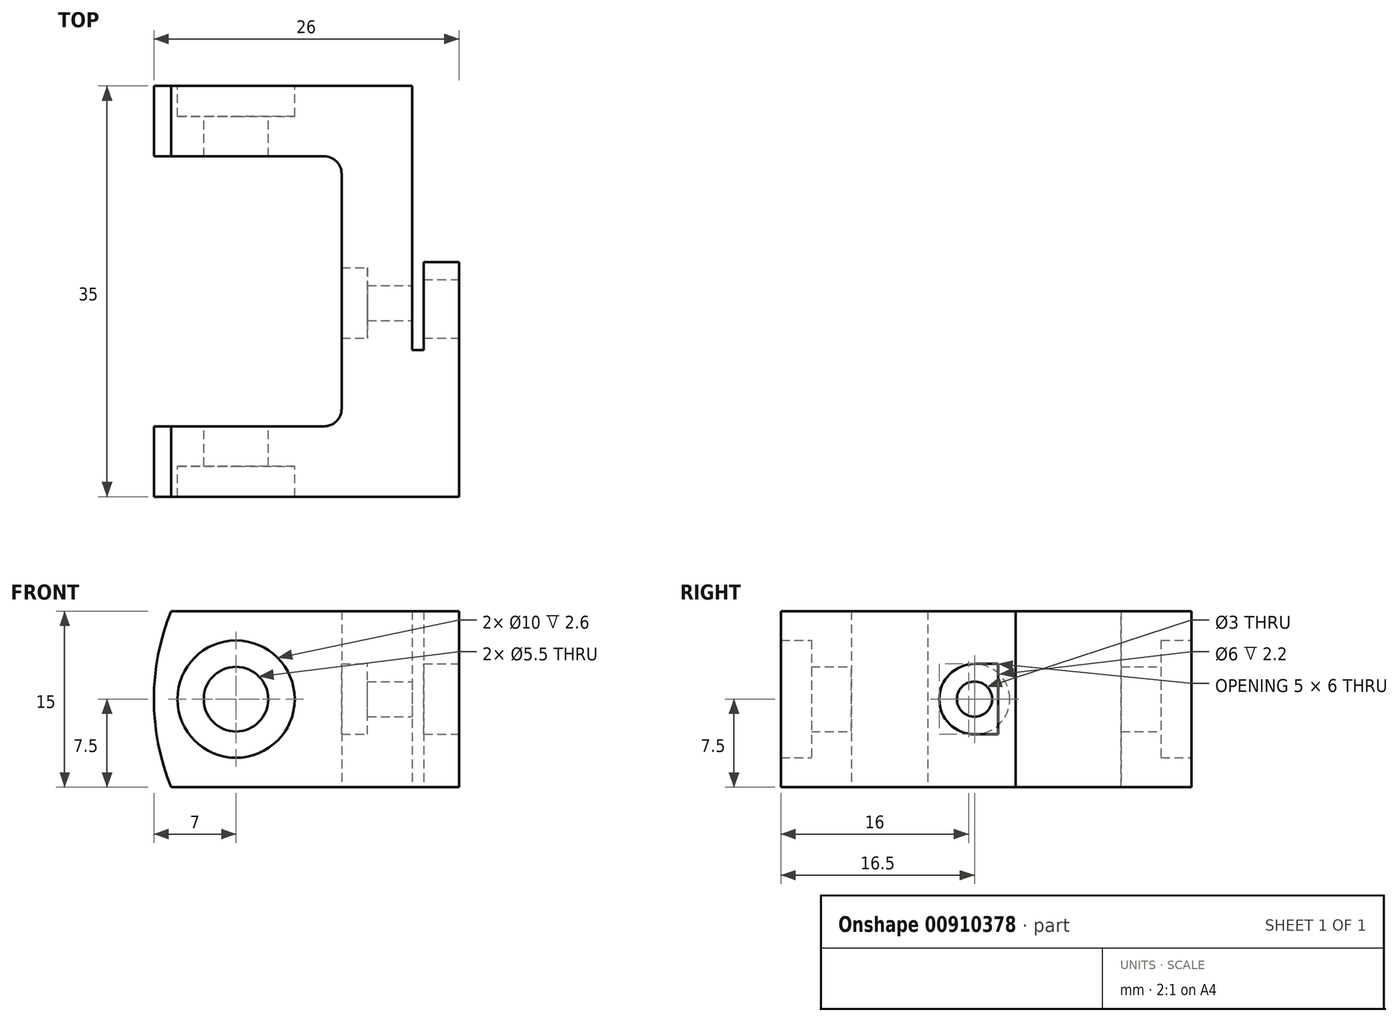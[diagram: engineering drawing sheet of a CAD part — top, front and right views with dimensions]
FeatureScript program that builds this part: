
annotation { "Feature Type Name" : "Feature", "Feature Type Description" : "" }
export const myFeature = defineFeature(function(context is Context, id is Id, definition is map)
    precondition{}
    {
        {
            var Q0;
            Q0=qCreatedBy(makeId("Top.planeOp"),FACE);
            var sketch = newSketch(context, id + "F0", { "sketchPlane" : qUnion([Q0])});
            skLineSegment(sketch, "E0", {"start": v(-16, 12.5) * mm, "end": v(-1.5, 12.5) * mm});
            skLineSegment(sketch, "E1", {"start": v(0, 11) * mm, "end": v(0, -9) * mm});
            skLineSegment(sketch, "E2", {"start": v(-1.5, -10.5) * mm, "end": v(-16, -10.5) * mm});
            skLineSegment(sketch, "E3", {"start": v(-16, -10.5) * mm, "end": v(-16, -16.5) * mm});
            skLineSegment(sketch, "E4", {"start": v(-16, -16.5) * mm, "end": v(10, -16.5) * mm});
            skLineSegment(sketch, "E5", {"start": v(10, -16.5) * mm, "end": v(10, 3.5) * mm});
            skLineSegment(sketch, "E6", {"start": v(10, 3.5) * mm, "end": v(7, 3.5) * mm});
            skLineSegment(sketch, "E7", {"start": v(7, 3.5) * mm, "end": v(7, -4) * mm});
            skLineSegment(sketch, "E8", {"start": v(7, -4) * mm, "end": v(6, -4) * mm});
            skLineSegment(sketch, "E9", {"start": v(6, -4) * mm, "end": v(6, 18.5) * mm});
            skLineSegment(sketch, "E10", {"start": v(6, 18.5) * mm, "end": v(-16, 18.5) * mm});
            skLineSegment(sketch, "E11", {"start": v(-16, 18.5) * mm, "end": v(-16, 12.5) * mm});
            skPoint(sketch, "E12.visualSharp", {"position": v(0, 12.5) * mm});
            skArc(sketch, "E12.filletArc", {"start": v(0, 11) * mm, "mid": v(-0.44, 12.06) * mm, "end": v(-1.5, 12.5) * mm});
            skPoint(sketch, "E13.visualSharp", {"position": v(0, -10.5) * mm});
            skArc(sketch, "E13.filletArc", {"start": v(-1.5, -10.5) * mm, "mid": v(-0.44, -10.06) * mm, "end": v(0, -9) * mm});
            skSolve(sketch);
        }
        {
            var Q0;
            Q0 = qSketchRegion(id + "F0", true);
            extrude(context, id + "F1", {"entities" : qUnion([Q0]), "depth" : 15 * mm, "offsetDistance" : 25.4 * mm, "symmetric" : true});
        }
        {
            var Q0;
            Q0=makeQuery(id+"F1.opExtrude","SWEPT_FACE",FACE,{"disambiguationData":[OSD([sQuery(id+"F0.wireOp",EDGE,"E1")])]});
            var sketch = newSketch(context, id + "F2", { "sketchPlane" : qUnion([Q0])});
            skPoint(sketch, "E14", {"position": v(0, 0) * mm});
            skSolve(sketch);
        }
        {
            var Q0;
            Q0=sQuery(id+"F2.wireOp",VERTEX,"E14");
            var Q1;
            Q1=makeQuery(id+"F1.opExtrude","SWEPT_BODY",BODY,{"disambiguationData":[OSD([sQuery(id+"F0.wireOp",EDGE,"E0"),sQuery(id+"F0.wireOp",EDGE,"E1"),sQuery(id+"F0.wireOp",EDGE,"E2"),sQuery(id+"F0.wireOp",EDGE,"E3"),sQuery(id+"F0.wireOp",EDGE,"E4"),sQuery(id+"F0.wireOp",EDGE,"E5"),sQuery(id+"F0.wireOp",EDGE,"E6"),sQuery(id+"F0.wireOp",EDGE,"E7"),sQuery(id+"F0.wireOp",EDGE,"E8"),sQuery(id+"F0.wireOp",EDGE,"E9"),sQuery(id+"F0.wireOp",EDGE,"E10"),sQuery(id+"F0.wireOp",EDGE,"E11"),sQuery(id+"F0.wireOp",EDGE,"E12.filletArc"),sQuery(id+"F0.wireOp",EDGE,"E13.filletArc")])]});
            hole(context, id + "F3", {"style" : HoleStyle.C_BORE, "endStyle" : HoleEndStyle.THROUGH, "holeDiameter" : 3 * mm, "cBoreDiameter" : 6 * mm, "cBoreDepth" : 2.2 * mm, "majorDiameter" : 6.35 * mm, "isTappedThrough" : true, "tappedDepth" : 12.7 * mm, "tapClearance" : 3, "locations" : qUnion([Q0]), "scope" : qUnion([Q1])});
        }
        {
            var Q0;
            Q0=makeQuery(id+"F1.opExtrude","SWEPT_FACE",FACE,{"disambiguationData":[OSD([sQuery(id+"F0.wireOp",EDGE,"E5")])]});
            var sketch = newSketch(context, id + "F4", { "sketchPlane" : qUnion([Q0])});
            skArc(sketch, "E15", {"start": v(0, 3) * mm, "mid": v(-3, 0) * mm, "end": v(0, -3) * mm});
            skLineSegment(sketch, "E16", {"start": v(0, 3) * mm, "end": v(2, 3) * mm});
            skLineSegment(sketch, "E17", {"start": v(2, 3) * mm, "end": v(2, -3) * mm});
            skLineSegment(sketch, "E18", {"start": v(2, -3) * mm, "end": v(0, -3) * mm});
            skSolve(sketch);
        }
        {
            var Q0;
            Q0 = qSketchRegion(id + "F4", true);
            var Q1;
            Q1=makeQuery(id+"F1.opExtrude","SWEPT_FACE",FACE,{"disambiguationData":[OSD([sQuery(id+"F0.wireOp",EDGE,"E7")])]});
            extrude(context, id + "F5", {"entities" : qUnion([Q0]), "operationType" : NewBodyOperationType.REMOVE, "endBound" : BoundingType.UP_TO_SURFACE, "oppositeDirection" : true, "depth" : 25.4 * mm, "endBoundEntityFace" : qUnion([Q1]), "offsetDistance" : 25.4 * mm});
        }
        {
            var Q0;
            Q0=qCreatedBy(makeId("Top.planeOp"),FACE);
            var sketch = newSketch(context, id + "F6", { "sketchPlane" : qUnion([Q0])});
            skLineSegment(sketch, "E19", {"start": v(-4, -16.5) * mm, "end": v(-4, -13.9) * mm});
            skLineSegment(sketch, "E20", {"start": v(-4, -13.9) * mm, "end": v(-6.25, -13.9) * mm});
            skLineSegment(sketch, "E21", {"start": v(-6.25, -13.9) * mm, "end": v(-6.25, 15.9) * mm});
            skLineSegment(sketch, "E22", {"start": v(-6.25, 15.9) * mm, "end": v(-4, 15.9) * mm});
            skLineSegment(sketch, "E23", {"start": v(-4, 15.9) * mm, "end": v(-4, 18.5) * mm});
            skLineSegment(sketch, "E24", {"start": v(-4, 18.5) * mm, "end": v(-9, 18.5) * mm});
            skLineSegment(sketch, "E25", {"start": v(-9, 18.5) * mm, "end": v(-9, -16.5) * mm});
            skLineSegment(sketch, "E26", {"start": v(-9, -16.5) * mm, "end": v(-4, -16.5) * mm});
            skLineSegment(sketch, "E27", {"start": v(-9, 18.5) * mm, "end": v(-9, 23.5) * mm, "construction": true});
            skSolve(sketch);
        }
        {
            var Q0;
            Q0 = qSketchRegion(id + "F6", true);
            var Q1;
            Q1=sQuery(id+"F6.wireOp",EDGE,"E27");
            revolve(context, id + "F7", {"operationType" : NewBodyOperationType.REMOVE, "surfaceOperationType" : NewSurfaceOperationType.NEW, "entities" : qUnion([Q0]), "axis" : qUnion([Q1]), "revolveType" : RevolveType.FULL, "oppositeDirection" : true});
        }
        {
            var Q0;
            Q0=qCreatedBy(makeId("Front.planeOp"),FACE);
            var sketch = newSketch(context, id + "F8", { "sketchPlane" : qUnion([Q0])});
            skArc(sketch, "E28", {"start": v(-14.54, 7.5) * mm, "mid": v(-16, 0) * mm, "end": v(-14.54, -7.5) * mm});
            skLineSegment(sketch, "E29", {"start": v(-14.54, -7.5) * mm, "end": v(-17.27, -7.5) * mm});
            skLineSegment(sketch, "E30", {"start": v(-17.27, -7.5) * mm, "end": v(-17.27, 7.5) * mm});
            skLineSegment(sketch, "E31", {"start": v(-17.27, 7.5) * mm, "end": v(-14.54, 7.5) * mm});
            skSolve(sketch);
        }
        {
            var Q0;
            Q0 = qSketchRegion(id + "F8", true);
            extrude(context, id + "F9", {"entities" : qUnion([Q0]), "operationType" : NewBodyOperationType.REMOVE, "endBound" : BoundingType.THROUGH_ALL, "oppositeDirection" : true, "depth" : 25.4 * mm, "offsetDistance" : 25.4 * mm, "hasSecondDirection" : true, "secondDirectionBound" : BoundingType.THROUGH_ALL, "secondDirectionOppositeDirection" : false, "secondDirectionDepth" : 25.4 * mm});
        }
    });
